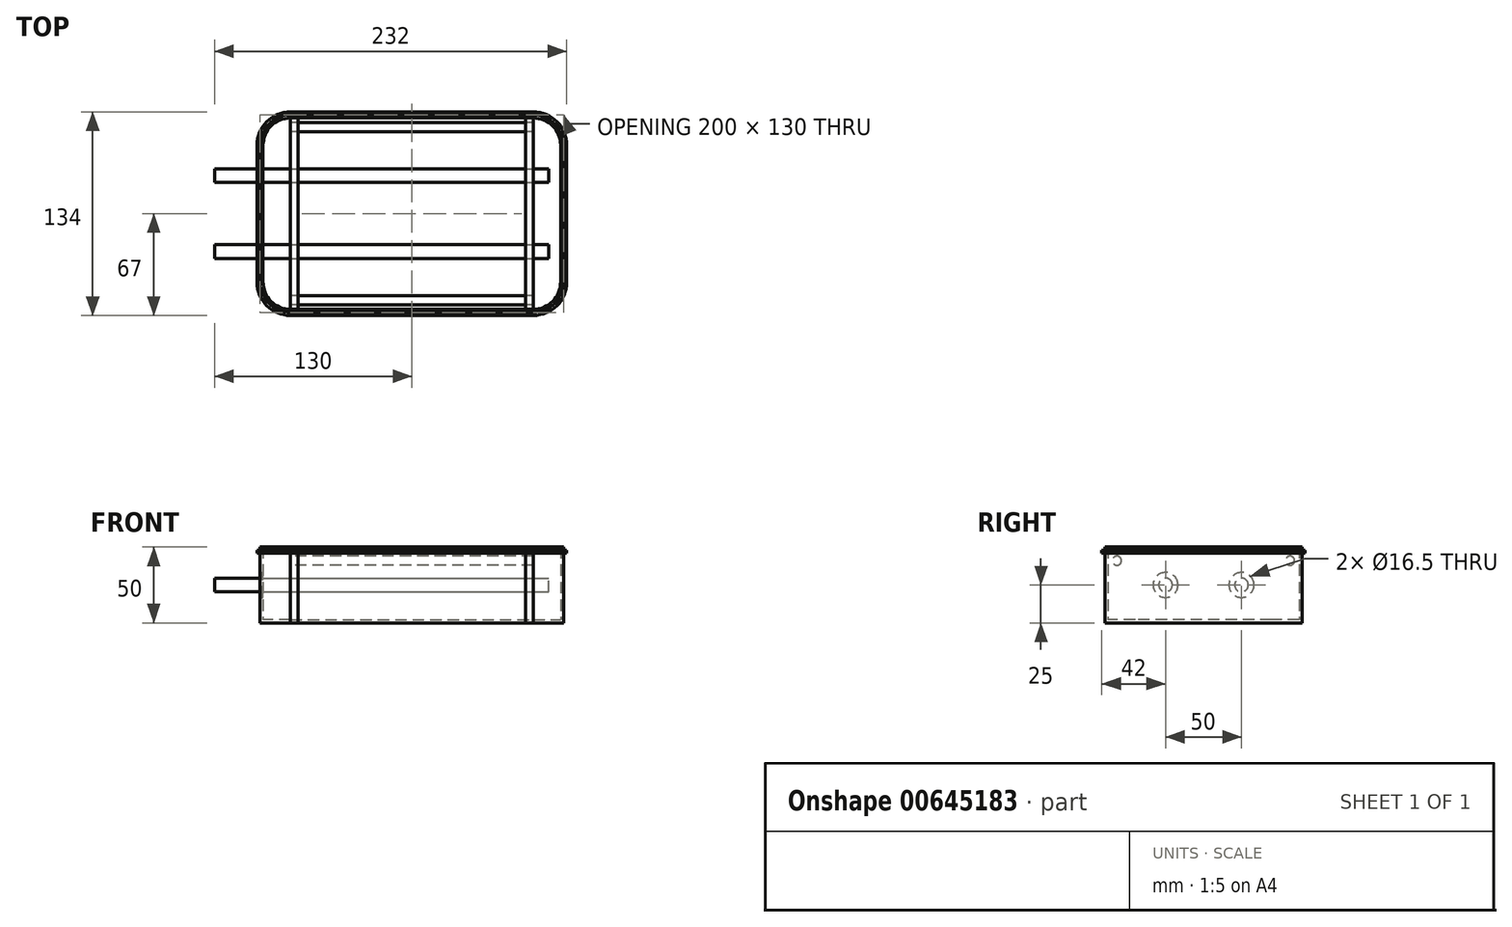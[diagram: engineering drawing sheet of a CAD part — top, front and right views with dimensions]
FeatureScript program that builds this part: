
annotation { "Feature Type Name" : "Feature", "Feature Type Description" : "" }
export const myFeature = defineFeature(function(context is Context, id is Id, definition is map)
    precondition{}
    {
        {
            var Q0;
            Q0=qCreatedBy(makeId("Top.planeOp"),FACE);
            var sketch = newSketch(context, id + "F0", { "sketchPlane" : qUnion([Q0])});
            skLineSegment(sketch, "E0.bottom", {"start": v(-80, 65) * mm, "end": v(80, 65) * mm});
            skLineSegment(sketch, "E0.top", {"start": v(-80, -65) * mm, "end": v(80, -65) * mm});
            skLineSegment(sketch, "E0.left", {"start": v(-100, 45) * mm, "end": v(-100, -45) * mm});
            skLineSegment(sketch, "E0.right", {"start": v(100, 45) * mm, "end": v(100, -45) * mm});
            skPoint(sketch, "E1.visualSharp", {"position": v(-100, 65) * mm});
            skArc(sketch, "E1.filletArc", {"start": v(-80, 65) * mm, "mid": v(-94.14, 59.14) * mm, "end": v(-100, 45) * mm});
            skPoint(sketch, "E2.visualSharp", {"position": v(100, 65) * mm});
            skArc(sketch, "E2.filletArc", {"start": v(100, 45) * mm, "mid": v(94.14, 59.14) * mm, "end": v(80, 65) * mm});
            skPoint(sketch, "E3.visualSharp", {"position": v(-100, -65) * mm});
            skArc(sketch, "E3.filletArc", {"start": v(-100, -45) * mm, "mid": v(-94.14, -59.14) * mm, "end": v(-80, -65) * mm});
            skPoint(sketch, "E4.visualSharp", {"position": v(100, -65) * mm});
            skArc(sketch, "E4.filletArc", {"start": v(80, -65) * mm, "mid": v(94.14, -59.14) * mm, "end": v(100, -45) * mm});
            skSolve(sketch);
        }
        {
            var Q0;
            Q0=qCreatedBy(makeId("Top.planeOp"),FACE);
            var sketch = newSketch(context, id + "F1", { "sketchPlane" : qUnion([Q0])});
            skLineSegment(sketch, "E5.bottom", {"start": v(-80, 67) * mm, "end": v(80, 67) * mm});
            skLineSegment(sketch, "E5.top", {"start": v(-80, -67) * mm, "end": v(80, -67) * mm});
            skLineSegment(sketch, "E5.left", {"start": v(-102, 45) * mm, "end": v(-102, -45) * mm});
            skLineSegment(sketch, "E5.right", {"start": v(102, 45) * mm, "end": v(102, -45) * mm});
            skPoint(sketch, "E6.visualSharp", {"position": v(-102, 67) * mm});
            skArc(sketch, "E6.filletArc", {"start": v(-80, 67) * mm, "mid": v(-95.56, 60.56) * mm, "end": v(-102, 45) * mm});
            skPoint(sketch, "E7.visualSharp", {"position": v(102, 67) * mm});
            skArc(sketch, "E7.filletArc", {"start": v(102, 45) * mm, "mid": v(95.56, 60.56) * mm, "end": v(80, 67) * mm});
            skPoint(sketch, "E8.visualSharp", {"position": v(-102, -67) * mm});
            skArc(sketch, "E8.filletArc", {"start": v(-102, -45) * mm, "mid": v(-95.56, -60.56) * mm, "end": v(-80, -67) * mm});
            skPoint(sketch, "E9.visualSharp", {"position": v(102, -67) * mm});
            skArc(sketch, "E9.filletArc", {"start": v(80, -67) * mm, "mid": v(95.56, -60.56) * mm, "end": v(102, -45) * mm});
            skSolve(sketch);
        }
        {
            var Q0;
            Q0=qCreatedBy(makeId("Top.planeOp"),FACE);
            var sketch = newSketch(context, id + "F2", { "sketchPlane" : qUnion([Q0])});
            skLineSegment(sketch, "E10.bottom", {"start": v(-80, 63) * mm, "end": v(80, 63) * mm});
            skLineSegment(sketch, "E10.top", {"start": v(-80, -63) * mm, "end": v(80, -63) * mm});
            skLineSegment(sketch, "E10.left", {"start": v(-98, 45) * mm, "end": v(-98, -45) * mm});
            skLineSegment(sketch, "E10.right", {"start": v(98, 45) * mm, "end": v(98, -45) * mm});
            skPoint(sketch, "E11.visualSharp", {"position": v(-98, 63) * mm});
            skArc(sketch, "E11.filletArc", {"start": v(-80, 63) * mm, "mid": v(-92.73, 57.73) * mm, "end": v(-98, 45) * mm});
            skPoint(sketch, "E12.visualSharp", {"position": v(98, 63) * mm});
            skArc(sketch, "E12.filletArc", {"start": v(98, 45) * mm, "mid": v(92.73, 57.73) * mm, "end": v(80, 63) * mm});
            skPoint(sketch, "E13.visualSharp", {"position": v(-98, -63) * mm});
            skArc(sketch, "E13.filletArc", {"start": v(-98, -45) * mm, "mid": v(-92.73, -57.73) * mm, "end": v(-80, -63) * mm});
            skPoint(sketch, "E14.visualSharp", {"position": v(98, -63) * mm});
            skArc(sketch, "E14.filletArc", {"start": v(80, -63) * mm, "mid": v(92.73, -57.73) * mm, "end": v(98, -45) * mm});
            skSolve(sketch);
        }
        {
            var Q0;
            Q0 = qSketchRegion(id + "F1", true);
            extrude(context, id + "F3", {"entities" : qUnion([Q0]), "depth" : 2 * mm, "offsetDistance" : 25 * mm});
        }
        {
            var Q0;
            Q0=makeQuery(id+"F3.opExtrude","SWEPT_BODY",BODY,{"disambiguationData":[OSD([sQuery(id+"F1.wireOp",EDGE,"E5.bottom"),sQuery(id+"F1.wireOp",EDGE,"E5.top"),sQuery(id+"F1.wireOp",EDGE,"E5.left"),sQuery(id+"F1.wireOp",EDGE,"E5.right"),sQuery(id+"F1.wireOp",EDGE,"E6.filletArc"),sQuery(id+"F1.wireOp",EDGE,"E7.filletArc"),sQuery(id+"F1.wireOp",EDGE,"E8.filletArc"),sQuery(id+"F1.wireOp",EDGE,"E9.filletArc")])]});
            var Q1;
            Q1=qCreatedBy(makeId("Top.planeOp"),FACE);
            transform(context, id + "F4", {"entities" : qUnion([Q0]), "transformType" : TransformType.TRANSLATION_DISTANCE, "transformDirection" : qUnion([Q1]), "distance" : 46 * mm, "makeCopy" : false});
        }
        {
            var Q0;
            Q0 = qSketchRegion(id + "F0", true);
            extrude(context, id + "F5", {"entities" : qUnion([Q0]), "operationType" : NewBodyOperationType.ADD, "depth" : 50 * mm, "offsetDistance" : 25 * mm});
        }
        {
            var Q0;
            Q0 = qSketchRegion(id + "F2", true);
            extrude(context, id + "F6", {"entities" : qUnion([Q0]), "depth" : 50 * mm, "offsetDistance" : 25 * mm});
        }
        {
            var Q0;
            Q0=makeQuery(id+"F6.opExtrude","SWEPT_BODY",BODY,{"disambiguationData":[OSD([sQuery(id+"F2.wireOp",EDGE,"E10.bottom"),sQuery(id+"F2.wireOp",EDGE,"E10.top"),sQuery(id+"F2.wireOp",EDGE,"E10.left"),sQuery(id+"F2.wireOp",EDGE,"E10.right"),sQuery(id+"F2.wireOp",EDGE,"E11.filletArc"),sQuery(id+"F2.wireOp",EDGE,"E12.filletArc"),sQuery(id+"F2.wireOp",EDGE,"E13.filletArc"),sQuery(id+"F2.wireOp",EDGE,"E14.filletArc")])]});
            var Q1;
            Q1=qCreatedBy(makeId("Top.planeOp"),FACE);
            transform(context, id + "F7", {"entities" : qUnion([Q0]), "transformType" : TransformType.TRANSLATION_DISTANCE, "transformDirection" : qUnion([Q1]), "distance" : 2 * mm, "makeCopy" : false});
        }
        {
            var Q0;
            Q0=makeQuery(id+"F6.opExtrude","SWEPT_BODY",BODY,{"disambiguationData":[OSD([sQuery(id+"F2.wireOp",EDGE,"E10.bottom"),sQuery(id+"F2.wireOp",EDGE,"E10.top"),sQuery(id+"F2.wireOp",EDGE,"E10.left"),sQuery(id+"F2.wireOp",EDGE,"E10.right"),sQuery(id+"F2.wireOp",EDGE,"E11.filletArc"),sQuery(id+"F2.wireOp",EDGE,"E12.filletArc"),sQuery(id+"F2.wireOp",EDGE,"E13.filletArc"),sQuery(id+"F2.wireOp",EDGE,"E14.filletArc")])]});
            var Q1;
            Q1=makeQuery(id+"F3.opExtrude","SWEPT_BODY",BODY,{"disambiguationData":[OSD([sQuery(id+"F1.wireOp",EDGE,"E5.bottom"),sQuery(id+"F1.wireOp",EDGE,"E5.top"),sQuery(id+"F1.wireOp",EDGE,"E5.left"),sQuery(id+"F1.wireOp",EDGE,"E5.right"),sQuery(id+"F1.wireOp",EDGE,"E6.filletArc"),sQuery(id+"F1.wireOp",EDGE,"E7.filletArc"),sQuery(id+"F1.wireOp",EDGE,"E8.filletArc"),sQuery(id+"F1.wireOp",EDGE,"E9.filletArc")])]});
            booleanBodies(context, id + "F8", {"operationType" : BooleanOperationType.SUBTRACTION, "tools" : qUnion([Q0]), "targets" : qUnion([Q1])});
        }
        {
            var Q0;
            Q0=qCreatedBy(makeId("Right.planeOp"),FACE);
            var sketch = newSketch(context, id + "F9", { "sketchPlane" : qUnion([Q0])});
            skLineSegment(sketch, "E15.bottom", {"start": v(-65, 48) * mm, "end": v(65, 48) * mm});
            skLineSegment(sketch, "E15.top", {"start": v(-65, 0) * mm, "end": v(65, 0) * mm});
            skLineSegment(sketch, "E15.left", {"start": v(-65, 48) * mm, "end": v(-65, 0) * mm});
            skLineSegment(sketch, "E15.right", {"start": v(65, 48) * mm, "end": v(65, 0) * mm});
            skSolve(sketch);
        }
        {
            var Q0;
            Q0=qCreatedBy(makeId("Right.planeOp"),FACE);
            var sketch = newSketch(context, id + "F10", { "sketchPlane" : qUnion([Q0])});
            skLineSegment(sketch, "E16.bottom", {"start": v(-65, 48) * mm, "end": v(65, 48) * mm});
            skLineSegment(sketch, "E16.top", {"start": v(-65, 0) * mm, "end": v(65, 0) * mm});
            skLineSegment(sketch, "E16.left", {"start": v(-65, 48) * mm, "end": v(-65, 0) * mm});
            skLineSegment(sketch, "E16.right", {"start": v(65, 48) * mm, "end": v(65, 0) * mm});
            skSolve(sketch);
        }
        {
            var Q0;
            Q0 = qSketchRegion(id + "F9", true);
            extrude(context, id + "F11", {"entities" : qUnion([Q0]), "depth" : 5 * mm, "offsetDistance" : 25 * mm});
        }
        {
            var Q0;
            Q0=makeQuery(id+"F11.opExtrude","SWEPT_BODY",BODY,{"disambiguationData":[OSD([sQuery(id+"F9.wireOp",EDGE,"E15.bottom"),sQuery(id+"F9.wireOp",EDGE,"E15.top"),sQuery(id+"F9.wireOp",EDGE,"E15.left"),sQuery(id+"F9.wireOp",EDGE,"E15.right")])]});
            var Q1;
            Q1=qCreatedBy(makeId("Right.planeOp"),FACE);
            transform(context, id + "F12", {"entities" : qUnion([Q0]), "transformType" : TransformType.TRANSLATION_DISTANCE, "transformDirection" : qUnion([Q1]), "distance" : 75 * mm, "makeCopy" : false});
        }
        {
            var Q0;
            Q0 = qSketchRegion(id + "F10", true);
            extrude(context, id + "F13", {"entities" : qUnion([Q0]), "oppositeDirection" : true, "depth" : 5 * mm, "offsetDistance" : 25 * mm});
        }
        {
            var Q0;
            Q0=makeQuery(id+"F13.opExtrude","SWEPT_BODY",BODY,{"disambiguationData":[OSD([sQuery(id+"F10.wireOp",EDGE,"E16.bottom"),sQuery(id+"F10.wireOp",EDGE,"E16.top"),sQuery(id+"F10.wireOp",EDGE,"E16.left"),sQuery(id+"F10.wireOp",EDGE,"E16.right")])]});
            var Q1;
            Q1=qCreatedBy(makeId("Right.planeOp"),FACE);
            transform(context, id + "F14", {"entities" : qUnion([Q0]), "transformType" : TransformType.TRANSLATION_DISTANCE, "transformDirection" : qUnion([Q1]), "distance" : 75 * mm, "oppositeDirection" : true, "makeCopy" : false});
        }
        {
            var Q0;
            Q0=qCreatedBy(makeId("Right.planeOp"),FACE);
            var sketch = newSketch(context, id + "F15", { "sketchPlane" : qUnion([Q0])});
            skCircle(sketch, "E17", {"center": v(25, 25) * mm, "radius": 5.25 * mm});
            skCircle(sketch, "E18", {"center": v(-25, 25) * mm, "radius": 5.25 * mm});
            skSolve(sketch);
        }
        {
            var Q0;
            Q0 = qSketchRegion(id + "F15", true);
            extrude(context, id + "F16", {"entities" : qUnion([Q0]), "depth" : 170 * mm, "offsetDistance" : 25 * mm, "symmetric" : true});
        }
        {
            var Q0;
            Q0=makeQuery(id+"F16.opExtrude","SWEPT_BODY",BODY,{"disambiguationData":[OSD([sQuery(id+"F15.wireOp",EDGE,"E17")])]});
            var Q1;
            Q1=makeQuery(id+"F16.opExtrude","SWEPT_BODY",BODY,{"disambiguationData":[OSD([sQuery(id+"F15.wireOp",EDGE,"E18")])]});
            var Q2;
            Q2=makeQuery(id+"F3.opExtrude","SWEPT_BODY",BODY,{"disambiguationData":[OSD([sQuery(id+"F1.wireOp",EDGE,"E5.bottom"),sQuery(id+"F1.wireOp",EDGE,"E5.top"),sQuery(id+"F1.wireOp",EDGE,"E5.left"),sQuery(id+"F1.wireOp",EDGE,"E5.right"),sQuery(id+"F1.wireOp",EDGE,"E6.filletArc"),sQuery(id+"F1.wireOp",EDGE,"E7.filletArc"),sQuery(id+"F1.wireOp",EDGE,"E8.filletArc"),sQuery(id+"F1.wireOp",EDGE,"E9.filletArc")])]});
            booleanBodies(context, id + "F17", {"operationType" : BooleanOperationType.SUBTRACTION, "tools" : qUnion([Q0, Q1]), "targets" : qUnion([Q2])});
        }
        {
            var Q0;
            Q0=qCreatedBy(makeId("Right.planeOp"),FACE);
            var sketch = newSketch(context, id + "F18", { "sketchPlane" : qUnion([Q0])});
            skCircle(sketch, "E19", {"center": v(25, 25) * mm, "radius": 8.25 * mm});
            skCircle(sketch, "E20", {"center": v(-25, 25) * mm, "radius": 8.25 * mm});
            skSolve(sketch);
        }
        {
            var Q0;
            Q0 = qSketchRegion(id + "F18", true);
            extrude(context, id + "F19", {"entities" : qUnion([Q0]), "oppositeDirection" : true, "depth" : 10 * mm, "offsetDistance" : 25 * mm});
        }
        {
            var Q0;
            Q0=makeQuery(id+"F19.opExtrude","SWEPT_BODY",BODY,{"disambiguationData":[OSD([sQuery(id+"F18.wireOp",EDGE,"E19")])]});
            var Q1;
            Q1=makeQuery(id+"F19.opExtrude","SWEPT_BODY",BODY,{"disambiguationData":[OSD([sQuery(id+"F18.wireOp",EDGE,"E20")])]});
            var Q2;
            Q2=qCreatedBy(makeId("Right.planeOp"),FACE);
            transform(context, id + "F20", {"entities" : qUnion([Q0, Q1]), "transformType" : TransformType.TRANSLATION_DISTANCE, "transformDirection" : qUnion([Q2]), "distance" : 95 * mm, "oppositeDirection" : true, "makeCopy" : false});
        }
        {
            var Q0;
            Q0=makeQuery(id+"F19.opExtrude","SWEPT_BODY",BODY,{"disambiguationData":[OSD([sQuery(id+"F18.wireOp",EDGE,"E19")])]});
            var Q1;
            Q1=makeQuery(id+"F19.opExtrude","SWEPT_BODY",BODY,{"disambiguationData":[OSD([sQuery(id+"F18.wireOp",EDGE,"E20")])]});
            var Q2;
            Q2=makeQuery(id+"F3.opExtrude","SWEPT_BODY",BODY,{"disambiguationData":[OSD([sQuery(id+"F1.wireOp",EDGE,"E5.bottom"),sQuery(id+"F1.wireOp",EDGE,"E5.top"),sQuery(id+"F1.wireOp",EDGE,"E5.left"),sQuery(id+"F1.wireOp",EDGE,"E5.right"),sQuery(id+"F1.wireOp",EDGE,"E6.filletArc"),sQuery(id+"F1.wireOp",EDGE,"E7.filletArc"),sQuery(id+"F1.wireOp",EDGE,"E8.filletArc"),sQuery(id+"F1.wireOp",EDGE,"E9.filletArc")])]});
            booleanBodies(context, id + "F21", {"operationType" : BooleanOperationType.SUBTRACTION, "tools" : qUnion([Q0, Q1]), "targets" : qUnion([Q2])});
        }
        {
            var Q0;
            Q0=qCreatedBy(makeId("Right.planeOp"),FACE);
            var sketch = newSketch(context, id + "F22", { "sketchPlane" : qUnion([Q0])});
            skCircle(sketch, "E21", {"center": v(25, 25) * mm, "radius": 4.5 * mm});
            skCircle(sketch, "E22", {"center": v(-25, 25) * mm, "radius": 4.5 * mm});
            skSolve(sketch);
        }
        {
            var Q0;
            Q0=makeQuery(id+"F22.imprint","IMPRINT",FACE,{"disambiguationData":[TD([[makeQuery(id+"F22.imprint","IMPRINT",EDGE,{"derivedFrom":sQuery(id+"F22.wireOp",EDGE,"E21")}),1.0]])]});
            var Q1;
            Q1=makeQuery(id+"F22.imprint","IMPRINT",FACE,{"disambiguationData":[TD([[makeQuery(id+"F22.imprint","IMPRINT",EDGE,{"derivedFrom":sQuery(id+"F22.wireOp",EDGE,"E22")}),1.0]])]});
            extrude(context, id + "F23", {"entities" : qUnion([Q0, Q1]), "oppositeDirection" : true, "depth" : 220 * mm, "offsetDistance" : 25 * mm});
        }
        {
            var Q0;
            Q0=makeQuery(id+"F23.opExtrude","SWEPT_BODY",BODY,{"disambiguationData":[OSD([sQuery(id+"F22.wireOp",EDGE,"E21")])]});
            var Q1;
            Q1=makeQuery(id+"F23.opExtrude","SWEPT_BODY",BODY,{"disambiguationData":[OSD([sQuery(id+"F22.wireOp",EDGE,"E22")])]});
            var Q2;
            Q2=qCreatedBy(makeId("Right.planeOp"),FACE);
            transform(context, id + "F24", {"entities" : qUnion([Q0, Q1]), "transformType" : TransformType.TRANSLATION_DISTANCE, "transformDirection" : qUnion([Q2]), "distance" : 90 * mm, "makeCopy" : false});
        }
        {
            var Q0;
            Q0=qCreatedBy(makeId("Right.planeOp"),FACE);
            var sketch = newSketch(context, id + "F25", { "sketchPlane" : qUnion([Q0])});
            skCircle(sketch, "E23", {"center": v(57, 41) * mm, "radius": 6 * mm});
            skCircle(sketch, "E24", {"center": v(-57, 41) * mm, "radius": 6 * mm});
            skSolve(sketch);
        }
        {
            var Q0;
            Q0 = qSketchRegion(id + "F25", true);
            extrude(context, id + "F26", {"entities" : qUnion([Q0]), "depth" : 160 * mm, "offsetDistance" : 25 * mm, "symmetric" : true});
        }
        {
            var Q0;
            Q0=qCreatedBy(makeId("Right.planeOp"),FACE);
            var sketch = newSketch(context, id + "F27", { "sketchPlane" : qUnion([Q0])});
            skCircle(sketch, "E25", {"center": v(57, 41) * mm, "radius": 3 * mm});
            skCircle(sketch, "E26", {"center": v(-57, 41) * mm, "radius": 3 * mm});
            skSolve(sketch);
        }
        {
            var Q0;
            Q0 = qSketchRegion(id + "F27", true);
            extrude(context, id + "F28", {"entities" : qUnion([Q0]), "depth" : 160 * mm, "offsetDistance" : 25 * mm, "symmetric" : true});
        }
        {
            var Q0;
            Q0=makeQuery(id+"F26.opExtrude","SWEPT_BODY",BODY,{"disambiguationData":[OSD([sQuery(id+"F25.wireOp",EDGE,"E23")])]});
            var Q1;
            Q1=makeQuery(id+"F26.opExtrude","SWEPT_BODY",BODY,{"disambiguationData":[OSD([sQuery(id+"F25.wireOp",EDGE,"E24")])]});
            var Q2;
            Q2=makeQuery(id+"F3.opExtrude","SWEPT_BODY",BODY,{"disambiguationData":[OSD([sQuery(id+"F1.wireOp",EDGE,"E5.bottom"),sQuery(id+"F1.wireOp",EDGE,"E5.top"),sQuery(id+"F1.wireOp",EDGE,"E5.left"),sQuery(id+"F1.wireOp",EDGE,"E5.right"),sQuery(id+"F1.wireOp",EDGE,"E6.filletArc"),sQuery(id+"F1.wireOp",EDGE,"E7.filletArc"),sQuery(id+"F1.wireOp",EDGE,"E8.filletArc"),sQuery(id+"F1.wireOp",EDGE,"E9.filletArc")])]});
            booleanBodies(context, id + "F29", {"operationType" : BooleanOperationType.SUBTRACTION, "tools" : qUnion([Q0, Q1]), "targets" : qUnion([Q2])});
        }
    });
